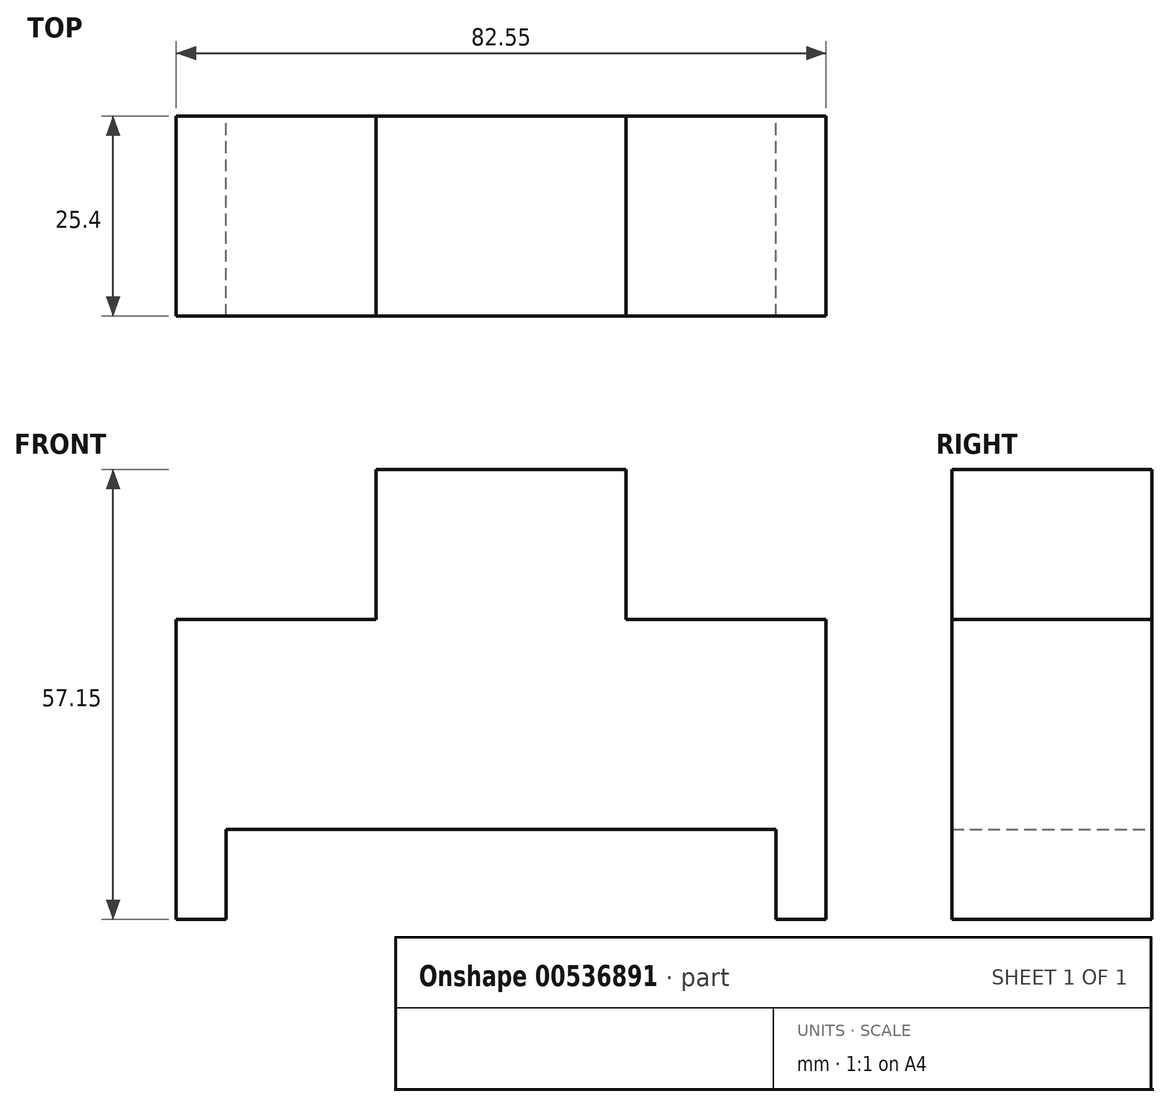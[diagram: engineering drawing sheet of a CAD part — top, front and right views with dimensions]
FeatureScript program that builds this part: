
annotation { "Feature Type Name" : "Feature", "Feature Type Description" : "" }
export const myFeature = defineFeature(function(context is Context, id is Id, definition is map)
    precondition{}
    {
        {
            var Q0;
            Q0=qCreatedBy(makeId("Front.planeOp"),FACE);
            var sketch = newSketch(context, id + "F0", { "sketchPlane" : qUnion([Q0])});
            skLineSegment(sketch, "E0", {"start": v(12.7, 5.08) * mm, "end": v(12.7, 11.43) * mm});
            skLineSegment(sketch, "E1", {"start": v(12.7, 11.43) * mm, "end": v(82.55, 11.43) * mm});
            skLineSegment(sketch, "E2", {"start": v(82.55, 11.43) * mm, "end": v(82.55, 0) * mm});
            skLineSegment(sketch, "E3", {"start": v(82.55, 0) * mm, "end": v(88.9, 0) * mm});
            skLineSegment(sketch, "E4", {"start": v(12.7, 5.08) * mm, "end": v(12.7, 0) * mm});
            skLineSegment(sketch, "E5", {"start": v(12.7, 0) * mm, "end": v(6.35, 0) * mm});
            skLineSegment(sketch, "E6", {"start": v(6.35, 0) * mm, "end": v(6.35, 38.1) * mm});
            skLineSegment(sketch, "E7", {"start": v(88.9, 0) * mm, "end": v(88.9, 38.1) * mm});
            skLineSegment(sketch, "E8", {"start": v(88.9, 38.1) * mm, "end": v(63.5, 38.1) * mm});
            skLineSegment(sketch, "E9", {"start": v(6.35, 38.1) * mm, "end": v(31.75, 38.1) * mm});
            skLineSegment(sketch, "E10", {"start": v(31.75, 38.1) * mm, "end": v(31.75, 57.15) * mm});
            skLineSegment(sketch, "E11", {"start": v(63.5, 38.1) * mm, "end": v(63.5, 57.15) * mm});
            skLineSegment(sketch, "E12", {"start": v(63.5, 57.15) * mm, "end": v(31.75, 57.15) * mm});
            skSolve(sketch);
        }
        {
            var Q0;
            Q0=makeQuery(id+"F0.imprint","IMPRINT",FACE,{"disambiguationData":[TD([[makeQuery(id+"F0.imprint","IMPRINT",EDGE,{"derivedFrom":sQuery(id+"F0.wireOp",EDGE,"E0")}),1.0]])]});
            extrude(context, id + "F1", {"entities" : qUnion([Q0]), "depth" : 25.4 * mm, "offsetDistance" : 25.4 * mm});
        }
    });
